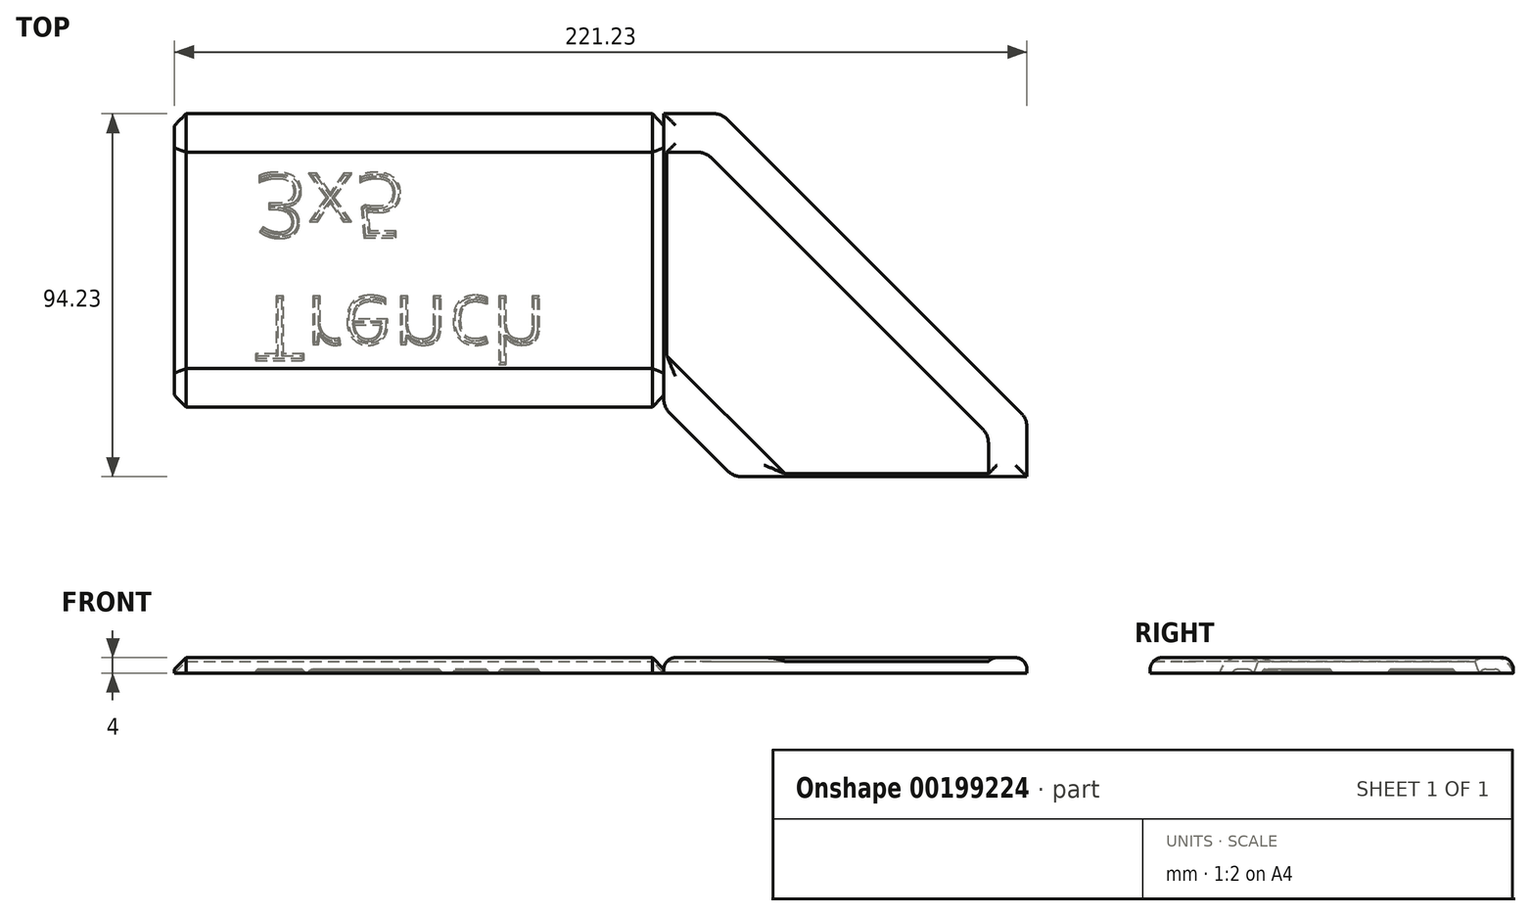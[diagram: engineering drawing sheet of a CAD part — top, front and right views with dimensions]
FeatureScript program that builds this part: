
annotation { "Feature Type Name" : "Feature", "Feature Type Description" : "" }
export const myFeature = defineFeature(function(context is Context, id is Id, definition is map)
    precondition{}
    {
        {
            var Q0;
            Q0=qCreatedBy(makeId("Top.planeOp"),FACE);
            var sketch = newSketch(context, id + "F0", { "sketchPlane" : qUnion([Q0])});
            skLineSegment(sketch, "E0.bottom", {"start": v(0, 0) * mm, "end": v(127, 0) * mm});
            skLineSegment(sketch, "E0.top", {"start": v(0, 76.2) * mm, "end": v(127, 76.2) * mm});
            skLineSegment(sketch, "E0.left", {"start": v(0, 0) * mm, "end": v(0, 76.2) * mm});
            skLineSegment(sketch, "E0.right", {"start": v(127, 0) * mm, "end": v(127, 76.2) * mm});
            skSolve(sketch);
        }
        {
            var Q0;
            Q0=makeQuery(id+"F0.imprint","IMPRINT",FACE,{"disambiguationData":[TD([[makeQuery(id+"F0.imprint","IMPRINT",EDGE,{"derivedFrom":sQuery(id+"F0.wireOp",EDGE,"E0.bottom")}),1.0]])]});
            extrude(context, id + "F1", {"entities" : qUnion([Q0]), "depth" : 3 * mm});
        }
        {
            var Q0;
            Q0=makeQuery(id+"F1.opExtrude","CAP_FACE",FACE,{"disambiguationData":[OSD([sQuery(id+"F0.wireOp",EDGE,"E0.bottom"),sQuery(id+"F0.wireOp",EDGE,"E0.top"),sQuery(id+"F0.wireOp",EDGE,"E0.left"),sQuery(id+"F0.wireOp",EDGE,"E0.right")])],"isStart":false});
            var sketch = newSketch(context, id + "F2", { "sketchPlane" : qUnion([Q0])});
            skLineSegment(sketch, "E1.bottom", {"start": v(0, 76.2) * mm, "end": v(127, 76.2) * mm});
            skLineSegment(sketch, "E1.top", {"start": v(0, 66.2) * mm, "end": v(127, 66.2) * mm});
            skLineSegment(sketch, "E1.left", {"start": v(0, 76.2) * mm, "end": v(0, 66.2) * mm});
            skLineSegment(sketch, "E1.right", {"start": v(127, 76.2) * mm, "end": v(127, 66.2) * mm});
            skLineSegment(sketch, "E2.bottom", {"start": v(0, 0) * mm, "end": v(127, 0) * mm});
            skLineSegment(sketch, "E2.top", {"start": v(0, 10) * mm, "end": v(127, 10) * mm});
            skLineSegment(sketch, "E2.left", {"start": v(0, 0) * mm, "end": v(0, 10) * mm});
            skLineSegment(sketch, "E2.right", {"start": v(127, 0) * mm, "end": v(127, 10) * mm});
            skSolve(sketch);
        }
        {
            var Q0;
            Q0 = qSketchRegion(id + "F2", true);
            extrude(context, id + "F3", {"entities" : qUnion([Q0]), "operationType" : NewBodyOperationType.ADD, "depth" : 1 * mm});
        }
        {
            var Q0;
            Q0=makeQuery(id+"F3.opExtrude","CAP_EDGE",EDGE,{"disambiguationData":[OSD([sQuery(id+"F2.wireOp",EDGE,"E1.top")])],"isStart":false});
            var Q1;
            Q1=makeQuery(id+"F3.opExtrude","CAP_EDGE",EDGE,{"disambiguationData":[OSD([sQuery(id+"F2.wireOp",EDGE,"E2.top")])],"isStart":false});
            var Q2;
            Q2=makeQuery(id+"F3.opExtrude","CAP_EDGE",EDGE,{"disambiguationData":[OSD([sQuery(id+"F2.wireOp",EDGE,"E2.bottom")])],"isStart":false});
            var Q3;
            Q3=makeQuery(id+"F3.opExtrude","CAP_EDGE",EDGE,{"disambiguationData":[OSD([sQuery(id+"F2.wireOp",EDGE,"E1.bottom")])],"isStart":false});
            fillet(context, id + "F4", {"entities" : qUnion([Q0, Q1, Q2, Q3]), "radius" : 5 * mm, "tangentPropagation" : true, "allowEdgeOverflow" : false});
        }
        {
            var Q0;
            Q0=makeQuery(id+"F1.opExtrude","CAP_EDGE",EDGE,{"disambiguationData":[OSD([sQuery(id+"F0.wireOp",EDGE,"E0.left")])],"isStart":false});
            var Q1;
            Q1=makeQuery(id+"F3.opExtrude","CAP_EDGE",EDGE,{"disambiguationData":[OSD([sQuery(id+"F2.wireOp",EDGE,"E2.left")])],"isStart":false});
            var Q2;
            Q2=makeQuery(id+"F4.opFillet","BLEND_EDGE",EDGE,{"blendedFrom":[makeQuery(id+"F3.opExtrude","CAP_EDGE",EDGE,{"disambiguationData":[OSD([sQuery(id+"F2.wireOp",EDGE,"E1.top")])],"isStart":false}),makeQuery(id+"F3.boolean.opBoolean","MERGE",FACE,{"derivedFrom":[makeQuery(id+"F1.opExtrude","SWEPT_FACE",FACE,{"disambiguationData":[OSD([sQuery(id+"F0.wireOp",EDGE,"E0.left")])]}),makeQuery(id+"F3.opExtrude","SWEPT_FACE",FACE,{"disambiguationData":[OSD([sQuery(id+"F2.wireOp",EDGE,"E1.left")])]}),makeQuery(id+"F3.opExtrude","SWEPT_FACE",FACE,{"disambiguationData":[OSD([sQuery(id+"F2.wireOp",EDGE,"E2.left")])]})]})],"blendedInto":[makeQuery(id+"F3.boolean.opBoolean","MERGE",FACE,{"derivedFrom":[makeQuery(id+"F1.opExtrude","SWEPT_FACE",FACE,{"disambiguationData":[OSD([sQuery(id+"F0.wireOp",EDGE,"E0.left")])]}),makeQuery(id+"F3.opExtrude","SWEPT_FACE",FACE,{"disambiguationData":[OSD([sQuery(id+"F2.wireOp",EDGE,"E1.left")])]}),makeQuery(id+"F3.opExtrude","SWEPT_FACE",FACE,{"disambiguationData":[OSD([sQuery(id+"F2.wireOp",EDGE,"E2.left")])]})]})]});
            var Q3;
            Q3=makeQuery(id+"F1.opExtrude","CAP_EDGE",EDGE,{"disambiguationData":[OSD([sQuery(id+"F0.wireOp",EDGE,"E0.right")])],"isStart":false});
            var Q4;
            Q4=makeQuery(id+"F3.opExtrude","CAP_EDGE",EDGE,{"disambiguationData":[OSD([sQuery(id+"F2.wireOp",EDGE,"E1.right")])],"isStart":false});
            var Q5;
            Q5=makeQuery(id+"F3.opExtrude","CAP_EDGE",EDGE,{"disambiguationData":[OSD([sQuery(id+"F2.wireOp",EDGE,"E2.right")])],"isStart":false});
            chamfer(context, id + "F5", {"entities" : qUnion([Q0, Q1, Q2, Q3, Q4, Q5]), "width" : 3 * mm, "tangentPropagation" : true});
        }
        {
            var Q0;
            Q0=makeQuery(id+"F1.opExtrude","CAP_FACE",FACE,{"disambiguationData":[OSD([sQuery(id+"F0.wireOp",EDGE,"E0.bottom"),sQuery(id+"F0.wireOp",EDGE,"E0.top"),sQuery(id+"F0.wireOp",EDGE,"E0.left"),sQuery(id+"F0.wireOp",EDGE,"E0.right")])],"isStart":true});
            var sketch = newSketch(context, id + "F6", { "sketchPlane" : qUnion([Q0])});
            skText(sketch, "E3", { "text": "Trench\n3x5", "fontName": "OpenSans-Regular.ttf"});
            const initialGuessF6  = {"E3": [0.02086, -0.02885, 1, 0, 0.0169]};
            skSetInitialGuess(sketch, initialGuessF6);
            skSolve(sketch);
        }
        {
            var Q0;
            Q0 = qSketchRegion(id + "F6", true);
            extrude(context, id + "F7", {"entities" : qUnion([Q0]), "operationType" : NewBodyOperationType.REMOVE, "oppositeDirection" : true, "depth" : 1 * mm});
        }
        {
            var Q0;
            Q0=makeQuery(id+"F7.boolean.opBoolean","COPY",FACE,{"derivedFrom":makeQuery(id+"F7.opExtrude","CAP_FACE",FACE,{"disambiguationData":[OSD([sQuery(id+"F6.wireOp",EDGE,"E3.sketch_text.stroke-130"),sQuery(id+"F6.wireOp",EDGE,"E3.sketch_text.stroke-131"),sQuery(id+"F6.wireOp",EDGE,"E3.sketch_text.stroke-132"),sQuery(id+"F6.wireOp",EDGE,"E3.sketch_text.stroke-133"),sQuery(id+"F6.wireOp",EDGE,"E3.sketch_text.stroke-134"),sQuery(id+"F6.wireOp",EDGE,"E3.sketch_text.stroke-135"),sQuery(id+"F6.wireOp",EDGE,"E3.sketch_text.stroke-136"),sQuery(id+"F6.wireOp",EDGE,"E3.sketch_text.stroke-137"),sQuery(id+"F6.wireOp",EDGE,"E3.sketch_text.stroke-138"),sQuery(id+"F6.wireOp",EDGE,"E3.sketch_text.stroke-139"),sQuery(id+"F6.wireOp",EDGE,"E3.sketch_text.stroke-140"),sQuery(id+"F6.wireOp",EDGE,"E3.sketch_text.stroke-141"),sQuery(id+"F6.wireOp",EDGE,"E3.sketch_text.stroke-142"),sQuery(id+"F6.wireOp",EDGE,"E3.sketch_text.stroke-143"),sQuery(id+"F6.wireOp",EDGE,"E3.sketch_text.stroke-144"),sQuery(id+"F6.wireOp",EDGE,"E3.sketch_text.stroke-145"),sQuery(id+"F6.wireOp",EDGE,"E3.sketch_text.stroke-146"),sQuery(id+"F6.wireOp",EDGE,"E3.sketch_text.stroke-147"),sQuery(id+"F6.wireOp",EDGE,"E3.sketch_text.stroke-148")])],"isStart":false})});
            var Q1;
            Q1=makeQuery(id+"F7.boolean.opBoolean","COPY",FACE,{"derivedFrom":makeQuery(id+"F7.opExtrude","CAP_FACE",FACE,{"disambiguationData":[OSD([sQuery(id+"F6.wireOp",EDGE,"E3.sketch_text.stroke-118"),sQuery(id+"F6.wireOp",EDGE,"E3.sketch_text.stroke-119"),sQuery(id+"F6.wireOp",EDGE,"E3.sketch_text.stroke-120"),sQuery(id+"F6.wireOp",EDGE,"E3.sketch_text.stroke-121"),sQuery(id+"F6.wireOp",EDGE,"E3.sketch_text.stroke-122"),sQuery(id+"F6.wireOp",EDGE,"E3.sketch_text.stroke-123"),sQuery(id+"F6.wireOp",EDGE,"E3.sketch_text.stroke-124"),sQuery(id+"F6.wireOp",EDGE,"E3.sketch_text.stroke-125"),sQuery(id+"F6.wireOp",EDGE,"E3.sketch_text.stroke-126"),sQuery(id+"F6.wireOp",EDGE,"E3.sketch_text.stroke-127"),sQuery(id+"F6.wireOp",EDGE,"E3.sketch_text.stroke-128"),sQuery(id+"F6.wireOp",EDGE,"E3.sketch_text.stroke-129")])],"isStart":false})});
            var Q2;
            Q2=makeQuery(id+"F7.boolean.opBoolean","COPY",FACE,{"derivedFrom":makeQuery(id+"F7.opExtrude","CAP_FACE",FACE,{"disambiguationData":[OSD([sQuery(id+"F6.wireOp",EDGE,"E3.sketch_text.stroke-90"),sQuery(id+"F6.wireOp",EDGE,"E3.sketch_text.stroke-91"),sQuery(id+"F6.wireOp",EDGE,"E3.sketch_text.stroke-92"),sQuery(id+"F6.wireOp",EDGE,"E3.sketch_text.stroke-93"),sQuery(id+"F6.wireOp",EDGE,"E3.sketch_text.stroke-94"),sQuery(id+"F6.wireOp",EDGE,"E3.sketch_text.stroke-95"),sQuery(id+"F6.wireOp",EDGE,"E3.sketch_text.stroke-96"),sQuery(id+"F6.wireOp",EDGE,"E3.sketch_text.stroke-97"),sQuery(id+"F6.wireOp",EDGE,"E3.sketch_text.stroke-98"),sQuery(id+"F6.wireOp",EDGE,"E3.sketch_text.stroke-99"),sQuery(id+"F6.wireOp",EDGE,"E3.sketch_text.stroke-100"),sQuery(id+"F6.wireOp",EDGE,"E3.sketch_text.stroke-101"),sQuery(id+"F6.wireOp",EDGE,"E3.sketch_text.stroke-102"),sQuery(id+"F6.wireOp",EDGE,"E3.sketch_text.stroke-103"),sQuery(id+"F6.wireOp",EDGE,"E3.sketch_text.stroke-104"),sQuery(id+"F6.wireOp",EDGE,"E3.sketch_text.stroke-105"),sQuery(id+"F6.wireOp",EDGE,"E3.sketch_text.stroke-106"),sQuery(id+"F6.wireOp",EDGE,"E3.sketch_text.stroke-107"),sQuery(id+"F6.wireOp",EDGE,"E3.sketch_text.stroke-108"),sQuery(id+"F6.wireOp",EDGE,"E3.sketch_text.stroke-109"),sQuery(id+"F6.wireOp",EDGE,"E3.sketch_text.stroke-110"),sQuery(id+"F6.wireOp",EDGE,"E3.sketch_text.stroke-111"),sQuery(id+"F6.wireOp",EDGE,"E3.sketch_text.stroke-112"),sQuery(id+"F6.wireOp",EDGE,"E3.sketch_text.stroke-113"),sQuery(id+"F6.wireOp",EDGE,"E3.sketch_text.stroke-114"),sQuery(id+"F6.wireOp",EDGE,"E3.sketch_text.stroke-115"),sQuery(id+"F6.wireOp",EDGE,"E3.sketch_text.stroke-116"),sQuery(id+"F6.wireOp",EDGE,"E3.sketch_text.stroke-117")])],"isStart":false})});
            var Q3;
            Q3=makeQuery(id+"F7.boolean.opBoolean","COPY",FACE,{"derivedFrom":makeQuery(id+"F7.opExtrude","CAP_FACE",FACE,{"disambiguationData":[OSD([sQuery(id+"F6.wireOp",EDGE,"E3.sketch_text.stroke-0"),sQuery(id+"F6.wireOp",EDGE,"E3.sketch_text.stroke-1"),sQuery(id+"F6.wireOp",EDGE,"E3.sketch_text.stroke-2"),sQuery(id+"F6.wireOp",EDGE,"E3.sketch_text.stroke-3"),sQuery(id+"F6.wireOp",EDGE,"E3.sketch_text.stroke-4"),sQuery(id+"F6.wireOp",EDGE,"E3.sketch_text.stroke-5"),sQuery(id+"F6.wireOp",EDGE,"E3.sketch_text.stroke-6"),sQuery(id+"F6.wireOp",EDGE,"E3.sketch_text.stroke-7")])],"isStart":false})});
            var Q4;
            Q4=makeQuery(id+"F7.boolean.opBoolean","COPY",FACE,{"derivedFrom":makeQuery(id+"F7.opExtrude","CAP_FACE",FACE,{"disambiguationData":[OSD([sQuery(id+"F6.wireOp",EDGE,"E3.sketch_text.stroke-8"),sQuery(id+"F6.wireOp",EDGE,"E3.sketch_text.stroke-9"),sQuery(id+"F6.wireOp",EDGE,"E3.sketch_text.stroke-10"),sQuery(id+"F6.wireOp",EDGE,"E3.sketch_text.stroke-11"),sQuery(id+"F6.wireOp",EDGE,"E3.sketch_text.stroke-12"),sQuery(id+"F6.wireOp",EDGE,"E3.sketch_text.stroke-13"),sQuery(id+"F6.wireOp",EDGE,"E3.sketch_text.stroke-14"),sQuery(id+"F6.wireOp",EDGE,"E3.sketch_text.stroke-15"),sQuery(id+"F6.wireOp",EDGE,"E3.sketch_text.stroke-16"),sQuery(id+"F6.wireOp",EDGE,"E3.sketch_text.stroke-17"),sQuery(id+"F6.wireOp",EDGE,"E3.sketch_text.stroke-18"),sQuery(id+"F6.wireOp",EDGE,"E3.sketch_text.stroke-19"),sQuery(id+"F6.wireOp",EDGE,"E3.sketch_text.stroke-20")])],"isStart":false})});
            var Q5;
            Q5=makeQuery(id+"F7.boolean.opBoolean","COPY",FACE,{"derivedFrom":makeQuery(id+"F7.opExtrude","CAP_FACE",FACE,{"disambiguationData":[OSD([sQuery(id+"F6.wireOp",EDGE,"E3.sketch_text.stroke-21"),sQuery(id+"F6.wireOp",EDGE,"E3.sketch_text.stroke-22"),sQuery(id+"F6.wireOp",EDGE,"E3.sketch_text.stroke-23"),sQuery(id+"F6.wireOp",EDGE,"E3.sketch_text.stroke-24"),sQuery(id+"F6.wireOp",EDGE,"E3.sketch_text.stroke-25"),sQuery(id+"F6.wireOp",EDGE,"E3.sketch_text.stroke-26"),sQuery(id+"F6.wireOp",EDGE,"E3.sketch_text.stroke-27"),sQuery(id+"F6.wireOp",EDGE,"E3.sketch_text.stroke-28"),sQuery(id+"F6.wireOp",EDGE,"E3.sketch_text.stroke-29"),sQuery(id+"F6.wireOp",EDGE,"E3.sketch_text.stroke-30"),sQuery(id+"F6.wireOp",EDGE,"E3.sketch_text.stroke-31"),sQuery(id+"F6.wireOp",EDGE,"E3.sketch_text.stroke-32"),sQuery(id+"F6.wireOp",EDGE,"E3.sketch_text.stroke-33"),sQuery(id+"F6.wireOp",EDGE,"E3.sketch_text.stroke-34"),sQuery(id+"F6.wireOp",EDGE,"E3.sketch_text.stroke-35"),sQuery(id+"F6.wireOp",EDGE,"E3.sketch_text.stroke-36"),sQuery(id+"F6.wireOp",EDGE,"E3.sketch_text.stroke-37"),sQuery(id+"F6.wireOp",EDGE,"E3.sketch_text.stroke-38"),sQuery(id+"F6.wireOp",EDGE,"E3.sketch_text.stroke-39")])],"isStart":false})});
            var Q6;
            Q6=makeQuery(id+"F7.boolean.opBoolean","COPY",FACE,{"derivedFrom":makeQuery(id+"F7.opExtrude","CAP_FACE",FACE,{"disambiguationData":[OSD([sQuery(id+"F6.wireOp",EDGE,"E3.sketch_text.stroke-40"),sQuery(id+"F6.wireOp",EDGE,"E3.sketch_text.stroke-41"),sQuery(id+"F6.wireOp",EDGE,"E3.sketch_text.stroke-42"),sQuery(id+"F6.wireOp",EDGE,"E3.sketch_text.stroke-43"),sQuery(id+"F6.wireOp",EDGE,"E3.sketch_text.stroke-44"),sQuery(id+"F6.wireOp",EDGE,"E3.sketch_text.stroke-45"),sQuery(id+"F6.wireOp",EDGE,"E3.sketch_text.stroke-46"),sQuery(id+"F6.wireOp",EDGE,"E3.sketch_text.stroke-47"),sQuery(id+"F6.wireOp",EDGE,"E3.sketch_text.stroke-48"),sQuery(id+"F6.wireOp",EDGE,"E3.sketch_text.stroke-49"),sQuery(id+"F6.wireOp",EDGE,"E3.sketch_text.stroke-50"),sQuery(id+"F6.wireOp",EDGE,"E3.sketch_text.stroke-51"),sQuery(id+"F6.wireOp",EDGE,"E3.sketch_text.stroke-52"),sQuery(id+"F6.wireOp",EDGE,"E3.sketch_text.stroke-53"),sQuery(id+"F6.wireOp",EDGE,"E3.sketch_text.stroke-54"),sQuery(id+"F6.wireOp",EDGE,"E3.sketch_text.stroke-55"),sQuery(id+"F6.wireOp",EDGE,"E3.sketch_text.stroke-56")])],"isStart":false})});
            var Q7;
            Q7=makeQuery(id+"F7.boolean.opBoolean","COPY",FACE,{"derivedFrom":makeQuery(id+"F7.opExtrude","CAP_FACE",FACE,{"disambiguationData":[OSD([sQuery(id+"F6.wireOp",EDGE,"E3.sketch_text.stroke-57"),sQuery(id+"F6.wireOp",EDGE,"E3.sketch_text.stroke-58"),sQuery(id+"F6.wireOp",EDGE,"E3.sketch_text.stroke-59"),sQuery(id+"F6.wireOp",EDGE,"E3.sketch_text.stroke-60"),sQuery(id+"F6.wireOp",EDGE,"E3.sketch_text.stroke-61"),sQuery(id+"F6.wireOp",EDGE,"E3.sketch_text.stroke-62"),sQuery(id+"F6.wireOp",EDGE,"E3.sketch_text.stroke-63"),sQuery(id+"F6.wireOp",EDGE,"E3.sketch_text.stroke-64"),sQuery(id+"F6.wireOp",EDGE,"E3.sketch_text.stroke-65"),sQuery(id+"F6.wireOp",EDGE,"E3.sketch_text.stroke-66"),sQuery(id+"F6.wireOp",EDGE,"E3.sketch_text.stroke-67"),sQuery(id+"F6.wireOp",EDGE,"E3.sketch_text.stroke-68"),sQuery(id+"F6.wireOp",EDGE,"E3.sketch_text.stroke-69"),sQuery(id+"F6.wireOp",EDGE,"E3.sketch_text.stroke-70"),sQuery(id+"F6.wireOp",EDGE,"E3.sketch_text.stroke-71")])],"isStart":false})});
            var Q8;
            Q8=makeQuery(id+"F7.boolean.opBoolean","COPY",FACE,{"derivedFrom":makeQuery(id+"F7.opExtrude","CAP_FACE",FACE,{"disambiguationData":[OSD([sQuery(id+"F6.wireOp",EDGE,"E3.sketch_text.stroke-72"),sQuery(id+"F6.wireOp",EDGE,"E3.sketch_text.stroke-73"),sQuery(id+"F6.wireOp",EDGE,"E3.sketch_text.stroke-74"),sQuery(id+"F6.wireOp",EDGE,"E3.sketch_text.stroke-75"),sQuery(id+"F6.wireOp",EDGE,"E3.sketch_text.stroke-76"),sQuery(id+"F6.wireOp",EDGE,"E3.sketch_text.stroke-77"),sQuery(id+"F6.wireOp",EDGE,"E3.sketch_text.stroke-78"),sQuery(id+"F6.wireOp",EDGE,"E3.sketch_text.stroke-79"),sQuery(id+"F6.wireOp",EDGE,"E3.sketch_text.stroke-80"),sQuery(id+"F6.wireOp",EDGE,"E3.sketch_text.stroke-81"),sQuery(id+"F6.wireOp",EDGE,"E3.sketch_text.stroke-82"),sQuery(id+"F6.wireOp",EDGE,"E3.sketch_text.stroke-83"),sQuery(id+"F6.wireOp",EDGE,"E3.sketch_text.stroke-84"),sQuery(id+"F6.wireOp",EDGE,"E3.sketch_text.stroke-85"),sQuery(id+"F6.wireOp",EDGE,"E3.sketch_text.stroke-86"),sQuery(id+"F6.wireOp",EDGE,"E3.sketch_text.stroke-87"),sQuery(id+"F6.wireOp",EDGE,"E3.sketch_text.stroke-88"),sQuery(id+"F6.wireOp",EDGE,"E3.sketch_text.stroke-89")])],"isStart":false})});
            chamfer(context, id + "F8", {"entities" : qUnion([Q0, Q1, Q2, Q3, Q4, Q5, Q6, Q7, Q8]), "width" : .5 * mm, "tangentPropagation" : true});
        }
        {
            var Q0;
            Q0=qCreatedBy(makeId("Top.planeOp"),FACE);
            var sketch = newSketch(context, id + "F9", { "sketchPlane" : qUnion([Q0])});
            skLineSegment(sketch, "E4", {"start": v(0, 0) * mm, "end": v(176.64, 0) * mm, "construction": true});
            skLineSegment(sketch, "E5", {"start": v(127, 0) * mm, "end": v(127, 76.2) * mm});
            skLineSegment(sketch, "E6", {"start": v(127, 76.2) * mm, "end": v(141.98, 76.2) * mm});
            skLineSegment(sketch, "E7", {"start": v(141.98, 76.2) * mm, "end": v(181.6, 36.58) * mm});
            skLineSegment(sketch, "E8", {"start": v(127, 0) * mm, "end": v(136.02, -9.02) * mm});
            skLineSegment(sketch, "E9", {"start": v(136.02, -9.02) * mm, "end": v(181.6, 36.58) * mm});
            skPoint(sketch, "E10.orphan", {"position": v(221.23, -3.05) * mm});
            skLineSegment(sketch, "E11.MirrorCS", {"start": v(221.23, -18.03) * mm, "end": v(221.23, -3.05) * mm});
            skLineSegment(sketch, "E12.MirrorCS", {"start": v(221.23, -3.05) * mm, "end": v(181.6, 36.58) * mm});
            skLineSegment(sketch, "E13.MirrorCS", {"start": v(145.03, -18.03) * mm, "end": v(136.02, -9.02) * mm});
            skLineSegment(sketch, "E14.MirrorCS", {"start": v(145.03, -18.03) * mm, "end": v(221.23, -18.03) * mm});
            skSolve(sketch);
        }
        {
            var Q0;
            Q0=makeQuery(id+"F9.imprint","IMPRINT",FACE,{"disambiguationData":[TD([[makeQuery(id+"F9.imprint","IMPRINT",EDGE,{"derivedFrom":sQuery(id+"F9.wireOp",EDGE,"E5")}),-1.0]])]});
            var Q1;
            Q1=makeQuery(id+"F9.imprint","IMPRINT",FACE,{"disambiguationData":[TD([[makeQuery(id+"F9.imprint","IMPRINT",EDGE,{"derivedFrom":sQuery(id+"F9.wireOp",EDGE,"E9")}),-1.0]])]});
            extrude(context, id + "F10", {"entities" : qUnion([Q0, Q1]), "depth" : 3 * mm});
        }
        {
            var Q0;
            Q0=makeQuery(id+"F10.opExtrude","CAP_FACE",FACE,{"disambiguationData":[OSD([sQuery(id+"F9.wireOp",EDGE,"E5"),sQuery(id+"F9.wireOp",EDGE,"E6"),sQuery(id+"F9.wireOp",EDGE,"E7"),sQuery(id+"F9.wireOp",EDGE,"E8"),sQuery(id+"F9.wireOp",EDGE,"E11.MirrorCS"),sQuery(id+"F9.wireOp",EDGE,"E12.MirrorCS"),sQuery(id+"F9.wireOp",EDGE,"E13.MirrorCS"),sQuery(id+"F9.wireOp",EDGE,"E14.MirrorCS")])],"isStart":false});
            var sketch = newSketch(context, id + "F11", { "sketchPlane" : qUnion([Q0])});
            skLineSegment(sketch, "E15", {"start": v(127, 66.2) * mm, "end": v(137.84, 66.2) * mm});
            skLineSegment(sketch, "E16", {"start": v(137.84, 66.2) * mm, "end": v(174.54, 29.5) * mm});
            skLineSegment(sketch, "E17", {"start": v(174.54, 29.5) * mm, "end": v(136.02, -9.02) * mm, "construction": true});
            skLineSegment(sketch, "E18", {"start": v(127, 14.14) * mm, "end": v(159.17, -18.03) * mm});
            skLineSegment(sketch, "E19.MirrorCS", {"start": v(211.23, -7.2) * mm, "end": v(174.54, 29.5) * mm});
            skLineSegment(sketch, "E20.MirrorCS", {"start": v(211.23, -18.03) * mm, "end": v(211.23, -7.2) * mm});
            skSolve(sketch);
        }
        {
            var Q0;
            {var subQ3=sQuery(id+"F11.wireOp",EDGE,"E15");Q0=makeQuery(id+"F11.imprint","IMPRINT",FACE,{"disambiguationData":[TD([[makeQuery(id+"F11.imprint","IMPRINT",EDGE,{"derivedFrom":subQ3}),1.0]])]});}
            var Q1;
            {var subQ0=sQuery(id+"F11.wireOp",EDGE,"E18");Q1=makeQuery(id+"F11.imprint","IMPRINT",FACE,{"disambiguationData":[TD([[makeQuery(id+"F11.imprint","IMPRINT",EDGE,{"derivedFrom":subQ0}),-1.0]])]});}
            extrude(context, id + "F12", {"entities" : qUnion([Q0, Q1]), "operationType" : NewBodyOperationType.ADD, "depth" : 1 * mm});
        }
        {
            var Q0;
            Q0=makeQuery(id+"F12.opExtrude","SWEPT_EDGE",EDGE,{"disambiguationData":[OSD([sQuery(id+"F11.wireOp",EDGE,"E15"),sQuery(id+"F11.wireOp",EDGE,"E16")])]});
            var Q1;
            Q1=makeQuery(id+"F12.opExtrude","SWEPT_EDGE",EDGE,{"disambiguationData":[OSD([sQuery(id+"F11.wireOp",EDGE,"E19.MirrorCS"),sQuery(id+"F11.wireOp",EDGE,"E20.MirrorCS")])]});
            var Q2;
            {var subQ0=sQuery(id+"F9.wireOp",EDGE,"E12.MirrorCS");var subQ1=sQuery(id+"F9.wireOp",EDGE,"E11.MirrorCS");Q2=makeQuery(id+"F12.boolean.opBoolean","MERGE",EDGE,{"derivedFrom":[makeQuery(id+"F10.opExtrude","SWEPT_EDGE",EDGE,{"disambiguationData":[OSD([subQ1,subQ0])]}),makeQuery(id+"F12.opExtrude","SWEPT_EDGE",EDGE,{"disambiguationData":[OSD([sQuery(id+"F9.wireOp",EDGE,"E7"),subQ1,subQ0])]})]});}
            var Q3;
            {var subQ0=sQuery(id+"F9.wireOp",EDGE,"E7");var subQ1=sQuery(id+"F9.wireOp",EDGE,"E6");Q3=makeQuery(id+"F12.boolean.opBoolean","MERGE",EDGE,{"derivedFrom":[makeQuery(id+"F10.opExtrude","SWEPT_EDGE",EDGE,{"disambiguationData":[OSD([subQ1,subQ0])]}),makeQuery(id+"F12.opExtrude","SWEPT_EDGE",EDGE,{"disambiguationData":[OSD([subQ1,subQ0,sQuery(id+"F9.wireOp",EDGE,"E12.MirrorCS")])]})]});}
            var Q4;
            {var subQ0=sQuery(id+"F9.wireOp",EDGE,"E14.MirrorCS");var subQ1=sQuery(id+"F9.wireOp",EDGE,"E13.MirrorCS");Q4=makeQuery(id+"F12.boolean.opBoolean","MERGE",EDGE,{"derivedFrom":[makeQuery(id+"F10.opExtrude","SWEPT_EDGE",EDGE,{"disambiguationData":[OSD([subQ1,subQ0])]}),makeQuery(id+"F12.opExtrude","SWEPT_EDGE",EDGE,{"disambiguationData":[OSD([sQuery(id+"F9.wireOp",EDGE,"E8"),subQ1,subQ0])]})]});}
            var Q5;
            {var subQ0=sQuery(id+"F9.wireOp",EDGE,"E8");var subQ1=sQuery(id+"F9.wireOp",EDGE,"E5");Q5=makeQuery(id+"F12.boolean.opBoolean","MERGE",EDGE,{"derivedFrom":[makeQuery(id+"F10.opExtrude","SWEPT_EDGE",EDGE,{"disambiguationData":[OSD([subQ1,subQ0])]}),makeQuery(id+"F12.opExtrude","SWEPT_EDGE",EDGE,{"disambiguationData":[OSD([subQ1,subQ0,sQuery(id+"F9.wireOp",EDGE,"E13.MirrorCS")])]})]});}
            fillet(context, id + "F13", {"entities" : qUnion([Q0, Q1, Q2, Q3, Q4, Q5]), "radius" : 5 * mm, "tangentPropagation" : true, "allowEdgeOverflow" : false});
        }
        {
            var Q0;
            Q0=makeQuery(id+"F12.opExtrude","CAP_EDGE",EDGE,{"disambiguationData":[OSD([sQuery(id+"F11.wireOp",EDGE,"E16"),sQuery(id+"F11.wireOp",EDGE,"E19.MirrorCS")])],"isStart":false});
            var Q1;
            Q1=makeQuery(id+"F12.opExtrude","CAP_EDGE",EDGE,{"disambiguationData":[OSD([sQuery(id+"F9.wireOp",EDGE,"E7"),sQuery(id+"F9.wireOp",EDGE,"E12.MirrorCS")])],"isStart":false});
            fillet(context, id + "F14", {"entities" : qUnion([Q0, Q1]), "radius" : 3 * mm, "tangentPropagation" : true, "allowEdgeOverflow" : false});
        }
        {
            var Q0;
            Q0=makeQuery(id+"F12.opExtrude","CAP_EDGE",EDGE,{"disambiguationData":[OSD([sQuery(id+"F11.wireOp",EDGE,"E18")])],"isStart":false});
            var Q1;
            Q1=makeQuery(id+"F12.opExtrude","CAP_EDGE",EDGE,{"disambiguationData":[OSD([sQuery(id+"F9.wireOp",EDGE,"E8"),sQuery(id+"F9.wireOp",EDGE,"E13.MirrorCS")])],"isStart":false});
            fillet(context, id + "F15", {"entities" : qUnion([Q0, Q1]), "radius" : 3 * mm, "tangentPropagation" : true, "allowEdgeOverflow" : false});
        }
    });
